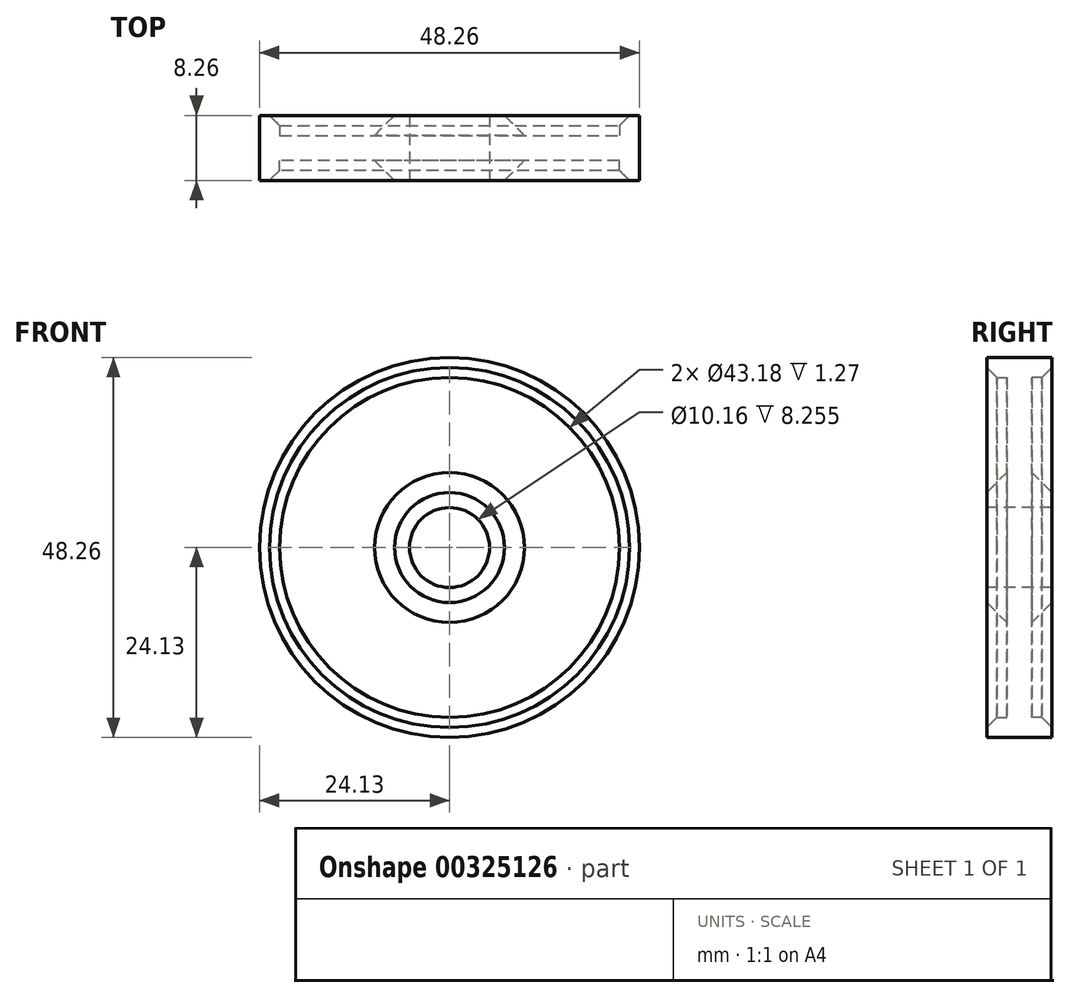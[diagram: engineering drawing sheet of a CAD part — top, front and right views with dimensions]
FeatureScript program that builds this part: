
annotation { "Feature Type Name" : "Feature", "Feature Type Description" : "" }
export const myFeature = defineFeature(function(context is Context, id is Id, definition is map)
    precondition{}
    {
        {
            var Q0;
            Q0=qCreatedBy(makeId("Top.planeOp"),FACE);
            var sketch = newSketch(context, id + "F0", { "sketchPlane" : qUnion([Q0])});
            skCircle(sketch, "E0", {"center": v(0, 0) * mm, "radius": 48.26 * mm});
            skSolve(sketch);
        }
        {
            var Q0;
            Q0 = qSketchRegion(id + "F0", true);
            extrude(context, id + "F1", {"entities" : qUnion([Q0]), "depth" : 6.35 * mm});
        }
        {
            var Q0;
            Q0=makeQuery(id+"F1.opExtrude","CAP_FACE",FACE,{"disambiguationData":[OSD([sQuery(id+"F0.wireOp",EDGE,"E0")])],"isStart":true});
            var sketch = newSketch(context, id + "F2", { "sketchPlane" : qUnion([Q0])});
            skCircle(sketch, "E1", {"center": v(0, 0) * mm, "radius": 48.26 * mm});
            skCircle(sketch, "E2", {"center": v(0, 0) * mm, "radius": 43.18 * mm});
            skSolve(sketch);
        }
        {
            var Q0;
            Q0=makeQuery(id+"F2.imprint","IMPRINT",FACE,{"disambiguationData":[TD([[makeQuery(id+"F2.imprint","IMPRINT",EDGE,{"derivedFrom":sQuery(id+"F2.wireOp",EDGE,"E1")}),-1.0]])]});
            extrude(context, id + "F3", {"entities" : qUnion([Q0]), "operationType" : NewBodyOperationType.ADD, "depth" : 5.08 * mm});
        }
        {
            var Q0;
            Q0=makeQuery(id+"F1.opExtrude","CAP_FACE",FACE,{"disambiguationData":[OSD([sQuery(id+"F0.wireOp",EDGE,"E0")])],"isStart":false});
            var sketch = newSketch(context, id + "F4", { "sketchPlane" : qUnion([Q0])});
            skCircle(sketch, "E3", {"center": v(0, 0) * mm, "radius": 48.26 * mm});
            skCircle(sketch, "E4", {"center": v(0, 0) * mm, "radius": 43.18 * mm});
            skSolve(sketch);
        }
        {
            var Q0;
            Q0=makeQuery(id+"F4.imprint","IMPRINT",FACE,{"disambiguationData":[TD([[makeQuery(id+"F4.imprint","IMPRINT",EDGE,{"derivedFrom":sQuery(id+"F4.wireOp",EDGE,"E3")}),1.0]])]});
            extrude(context, id + "F5", {"entities" : qUnion([Q0]), "operationType" : NewBodyOperationType.ADD, "depth" : 5.08 * mm});
        }
        {
            var Q0;
            Q0=makeQuery(id+"F1.opExtrude","CAP_FACE",FACE,{"disambiguationData":[OSD([sQuery(id+"F0.wireOp",EDGE,"E0")])],"isStart":true});
            var sketch = newSketch(context, id + "F6", { "sketchPlane" : qUnion([Q0])});
            skCircle(sketch, "E5", {"center": v(0, 0) * mm, "radius": 12.7 * mm});
            skSolve(sketch);
        }
        {
            var Q0;
            Q0=makeQuery(id+"F1.opExtrude","CAP_FACE",FACE,{"disambiguationData":[OSD([sQuery(id+"F0.wireOp",EDGE,"E0")])],"isStart":true});
            var sketch = newSketch(context, id + "F7", { "sketchPlane" : qUnion([Q0])});
            skCircle(sketch, "E6", {"center": v(0, 0) * mm, "radius": 19.05 * mm});
            skSolve(sketch);
        }
        {
            var Q0;
            Q0=makeQuery(id+"F7.imprint","IMPRINT",FACE,{"disambiguationData":[TD([[makeQuery(id+"F7.imprint","IMPRINT",EDGE,{"derivedFrom":sQuery(id+"F7.wireOp",EDGE,"E6")}),1.0]])]});
            extrude(context, id + "F8", {"entities" : qUnion([Q0]), "operationType" : NewBodyOperationType.ADD, "depth" : 5.08 * mm});
        }
        {
            var Q0;
            Q0=makeQuery(id+"F8.opExtrude","CAP_EDGE",EDGE,{"disambiguationData":[OSD([sQuery(id+"F7.wireOp",EDGE,"E6")])],"isStart":false});
            chamfer(context, id + "F9", {"entities" : qUnion([Q0]), "width" : 5.08 * mm, "tangentPropagation" : true});
        }
        {
            var Q0;
            Q0=makeQuery(id+"F1.opExtrude","CAP_FACE",FACE,{"disambiguationData":[OSD([sQuery(id+"F0.wireOp",EDGE,"E0")])],"isStart":false});
            var sketch = newSketch(context, id + "F10", { "sketchPlane" : qUnion([Q0])});
            skCircle(sketch, "E7", {"center": v(0, 0) * mm, "radius": 19.05 * mm});
            skSolve(sketch);
        }
        {
            var Q0;
            Q0=makeQuery(id+"F10.imprint","IMPRINT",FACE,{"disambiguationData":[TD([[makeQuery(id+"F10.imprint","IMPRINT",EDGE,{"derivedFrom":sQuery(id+"F10.wireOp",EDGE,"E7")}),1.0]])]});
            extrude(context, id + "F11", {"entities" : qUnion([Q0]), "operationType" : NewBodyOperationType.ADD, "depth" : 5.08 * mm});
        }
        {
            var Q0;
            Q0=makeQuery(id+"F11.opExtrude","CAP_EDGE",EDGE,{"disambiguationData":[OSD([sQuery(id+"F10.wireOp",EDGE,"E7")])],"isStart":false});
            chamfer(context, id + "F12", {"entities" : qUnion([Q0]), "width" : 5.08 * mm, "tangentPropagation" : true});
        }
        {
            var Q0;
            Q0=makeQuery(id+"F11.opExtrude","CAP_FACE",FACE,{"disambiguationData":[OSD([sQuery(id+"F10.wireOp",EDGE,"E7")])],"isStart":false});
            var sketch = newSketch(context, id + "F13", { "sketchPlane" : qUnion([Q0])});
            skCircle(sketch, "E8", {"center": v(0, 0) * mm, "radius": 10.16 * mm});
            skSolve(sketch);
        }
        {
            var Q0;
            Q0=makeQuery(id+"F13.imprint","IMPRINT",FACE,{"disambiguationData":[TD([[makeQuery(id+"F13.imprint","IMPRINT",EDGE,{"derivedFrom":sQuery(id+"F13.wireOp",EDGE,"E8")}),1.0]])]});
            extrude(context, id + "F14", {"entities" : qUnion([Q0]), "operationType" : NewBodyOperationType.REMOVE, "oppositeDirection" : true, "depth" : 25.4 * mm});
        }
        {
            var Q0;
            Q0=makeQuery(id+"F3.opExtrude","CAP_EDGE",EDGE,{"disambiguationData":[OSD([sQuery(id+"F2.wireOp",EDGE,"E2")])],"isStart":false});
            var Q1;
            Q1=makeQuery(id+"F5.opExtrude","CAP_EDGE",EDGE,{"disambiguationData":[OSD([sQuery(id+"F4.wireOp",EDGE,"E4")])],"isStart":false});
            chamfer(context, id + "F15", {"entities" : qUnion([Q0, Q1]), "width" : 2.54 * mm, "tangentPropagation" : true});
        }
        {
            var Q0;
            Q0=qCreatedBy(makeId("Top.planeOp"),FACE);
            var sketch = newSketch(context, id + "F16", { "sketchPlane" : qUnion([Q0])});
            skLineSegment(sketch, "E9", {"start": v(2.74, 0) * mm, "end": v(54.25, 0) * mm});
            skSolve(sketch);
        }
        {
            var Q0;
            Q0=makeQuery(id+"F1.opExtrude","SWEPT_BODY",BODY,{"disambiguationData":[OSD([sQuery(id+"F0.wireOp",EDGE,"E0")])]});
            var Q1;
            Q1=sQuery(id+"F16.wireOp",EDGE,"E9");
            transform(context, id + "F17", {"entities" : qUnion([Q0]), "transformType" : TransformType.ROTATION, "transformAxis" : qUnion([Q1]), "angle" : 90 * degree, "makeCopy" : false});
        }
        {
            var Q0;
            Q0=makeQuery(id+"F1.opExtrude","SWEPT_BODY",BODY,{"disambiguationData":[OSD([sQuery(id+"F0.wireOp",EDGE,"E0")])]});
            var Q1;
            Q1=sQuery(id+"F6.wireOp",VERTEX,"E5.center");
            transform(context, id + "F18", {"entities" : qUnion([Q0]), "transformType" : TransformType.SCALE_UNIFORMLY, "scale" : .5, "scalePoint" : qUnion([Q1]), "makeCopy" : false});
        }
    });
